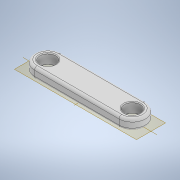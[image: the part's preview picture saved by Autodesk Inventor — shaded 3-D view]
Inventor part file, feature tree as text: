
AUTODESK INVENTOR PART (.ipt)
format: ipt  version: 2020 (Build 240168000, 168)  size: 153,088 bytes
history: native  units: mm
features: fillet x2, other x1, extrude x1, sketch x1
ambient origin geometry x8: Origin, YZ Plane, XZ Plane, XY Plane, X Axis, Y Axis, Z Axis, Center Point
bodies: Body1 (feature_tree)
feature tree (5):
  other  "Твердое тело1"
  extrude  "Выдавливание1"  Depth=32.0mm
  fillet  "Сопряжение1"  Radius=10.0mm
  fillet  "Сопряжение2"  Radius=6.0mm
  sketch  "Эскиз1"
